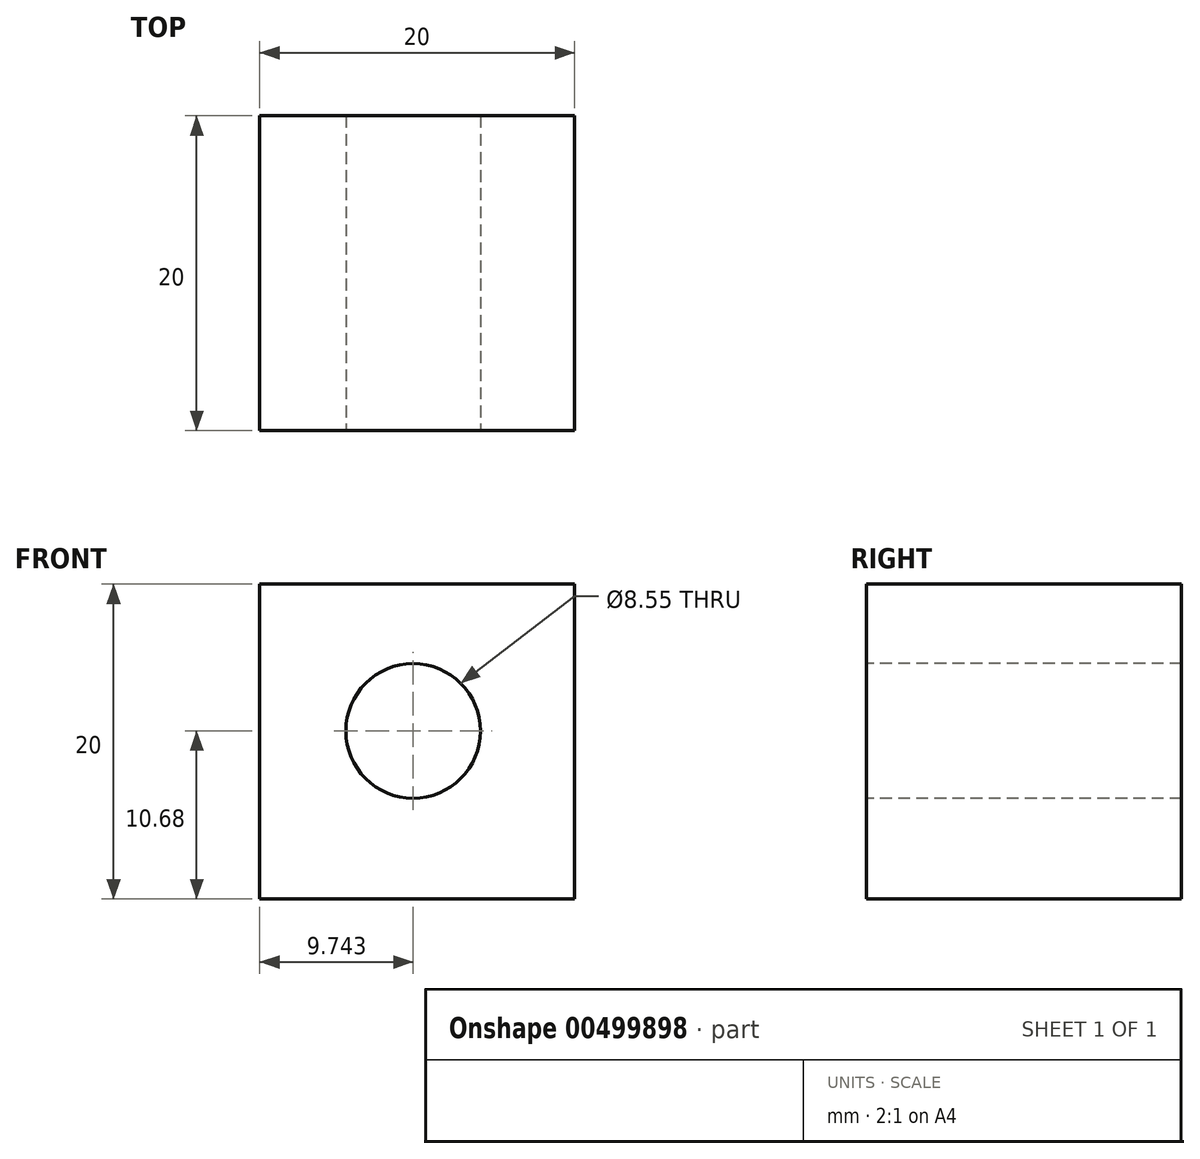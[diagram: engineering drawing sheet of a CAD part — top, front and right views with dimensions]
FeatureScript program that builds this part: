
annotation { "Feature Type Name" : "Feature", "Feature Type Description" : "" }
export const myFeature = defineFeature(function(context is Context, id is Id, definition is map)
    precondition{}
    {
        {
            var Q0;
            Q0=qCreatedBy(makeId("Front.planeOp"),FACE);
            var sketch = newSketch(context, id + "F0", { "sketchPlane" : qUnion([Q0])});
            skLineSegment(sketch, "E0.bottom", {"start": v(0, 0) * mm, "end": v(20, 0) * mm});
            skLineSegment(sketch, "E0.top", {"start": v(0, 20) * mm, "end": v(20, 20) * mm});
            skLineSegment(sketch, "E0.left", {"start": v(0, 0) * mm, "end": v(0, 20) * mm});
            skLineSegment(sketch, "E0.right", {"start": v(20, 0) * mm, "end": v(20, 20) * mm});
            skSolve(sketch);
        }
        {
            var Q0;
            Q0 = qSketchRegion(id + "F0", true);
            extrude(context, id + "F1", {"entities" : qUnion([Q0]), "depth" : 20 * mm});
        }
        {
            var Q0;
            Q0=makeQuery(id+"F1.opExtrude","CAP_FACE",FACE,{"disambiguationData":[OSD([sQuery(id+"F0.wireOp",EDGE,"E0.bottom"),sQuery(id+"F0.wireOp",EDGE,"E0.top"),sQuery(id+"F0.wireOp",EDGE,"E0.left"),sQuery(id+"F0.wireOp",EDGE,"E0.right")])],"isStart":false});
            var sketch = newSketch(context, id + "F2", { "sketchPlane" : qUnion([Q0])});
            skPoint(sketch, "E1", {"position": v(10, 0) * mm});
            skPoint(sketch, "E2", {"position": v(9.74, 10.68) * mm});
            skCircle(sketch, "E3", {"center": v(9.74, 10.68) * mm, "radius": 4.27 * mm});
            skSolve(sketch);
        }
        {
            var Q0;
            Q0 = qSketchRegion(id + "F2", true);
            extrude(context, id + "F3", {"entities" : qUnion([Q0]), "operationType" : NewBodyOperationType.REMOVE, "oppositeDirection" : true, "depth" : 25 * mm});
        }
    });
